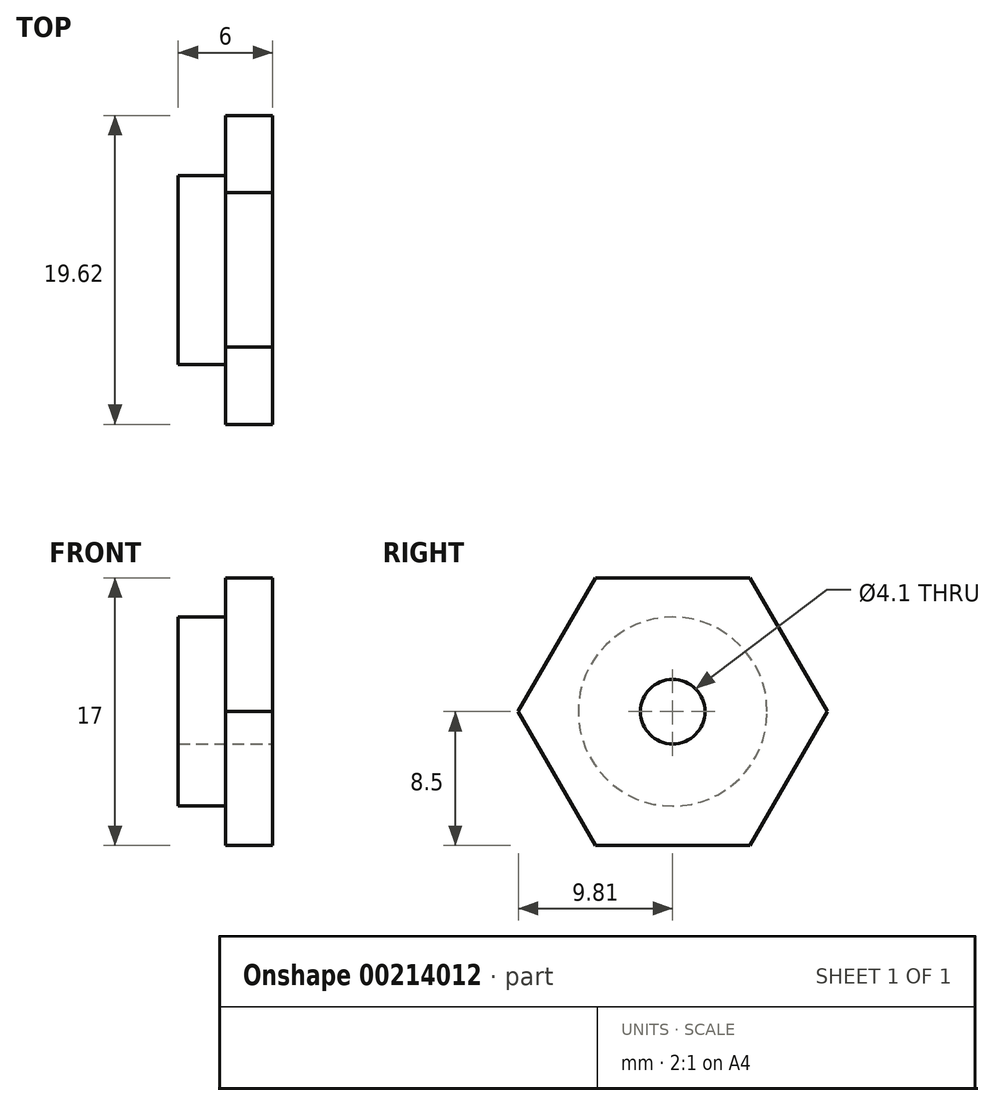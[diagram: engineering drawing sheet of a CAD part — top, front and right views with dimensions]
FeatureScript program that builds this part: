
annotation { "Feature Type Name" : "Feature", "Feature Type Description" : "" }
export const myFeature = defineFeature(function(context is Context, id is Id, definition is map)
    precondition{}
    {
        {
            var Q0;
            Q0=qCreatedBy(makeId("Right.planeOp"),FACE);
            var sketch = newSketch(context, id + "F0", { "sketchPlane" : qUnion([Q0])});
            skCircle(sketch, "E0", {"center": v(0, 0) * mm, "radius": 6 * mm});
            skSolve(sketch);
        }
        {
            var Q0;
            Q0 = qSketchRegion(id + "F0", true);
            extrude(context, id + "F1", {"entities" : qUnion([Q0]), "depth" : 3 * mm});
        }
        {
            var Q0;
            Q0=makeQuery(id+"F1.opExtrude","CAP_FACE",FACE,{"disambiguationData":[OSD([sQuery(id+"F0.wireOp",EDGE,"E0")])],"isStart":false});
            var sketch = newSketch(context, id + "F2", { "sketchPlane" : qUnion([Q0])});
            skCircle(sketch, "E1.cCircle", {"center": v(0, 0) * mm, "radius": 8.5 * mm, "construction": true});
            skLineSegment(sketch, "E1.0", {"start": v(-4.9, 8.5) * mm, "end": v(4.9, 8.5) * mm});
            skLineSegment(sketch, "E1.1", {"start": v(4.9, 8.5) * mm, "end": v(9.81, 0) * mm});
            skLineSegment(sketch, "E1.2", {"start": v(9.81, 0) * mm, "end": v(4.9, -8.5) * mm});
            skLineSegment(sketch, "E1.3", {"start": v(4.9, -8.5) * mm, "end": v(-4.9, -8.5) * mm});
            skLineSegment(sketch, "E1.4", {"start": v(-4.9, -8.5) * mm, "end": v(-9.81, 0) * mm});
            skLineSegment(sketch, "E1.5", {"start": v(-9.81, 0) * mm, "end": v(-4.9, 8.5) * mm});
            skPoint(sketch, "E1.0.midPoint", {"position": v(0, 8.5) * mm});
            skSolve(sketch);
        }
        {
            var Q0;
            Q0 = qSketchRegion(id + "F2", true);
            extrude(context, id + "F3", {"entities" : qUnion([Q0]), "operationType" : NewBodyOperationType.ADD, "depth" : 3 * mm});
        }
        {
            var Q0;
            Q0=makeQuery(id+"F3.opExtrude","CAP_FACE",FACE,{"disambiguationData":[OSD([sQuery(id+"F2.wireOp",EDGE,"E1.0"),sQuery(id+"F2.wireOp",EDGE,"E1.1"),sQuery(id+"F2.wireOp",EDGE,"E1.2"),sQuery(id+"F2.wireOp",EDGE,"E1.3"),sQuery(id+"F2.wireOp",EDGE,"E1.4"),sQuery(id+"F2.wireOp",EDGE,"E1.5")])],"isStart":false});
            var sketch = newSketch(context, id + "F4", { "sketchPlane" : qUnion([Q0])});
            skPoint(sketch, "E2", {"position": v(0, 0) * mm});
            skSolve(sketch);
        }
        {
            var Q0;
            Q0=sQuery(id+"F4.wireOp",VERTEX,"E2");
            var Q1;
            Q1=makeQuery(id+"F1.opExtrude","SWEPT_BODY",BODY,{"disambiguationData":[OSD([sQuery(id+"F0.wireOp",EDGE,"E0")])]});
            hole(context, id + "F5", {"style" : HoleStyle.SIMPLE, "endStyle" : HoleEndStyle.THROUGH, "standardTappedOrClearance" : lookupTablePath({ "standard" : "ISO", "engagement" : "75%", "pitch" : "0.9 mm", "size" : "M5", "type" : "Tapped" }), "standardBlindInLast" : lookupTablePath({ "standard" : "ISO", "engagement" : "75%", "pitch" : "0.9 mm", "size" : "M5", "type" : "Tapped" }), "holeDiameter" : 4.1 * mm, "locations" : qUnion([Q0]), "scope" : qUnion([Q1]), "isTappedThrough" : true, "showTappedDepth" : true});
        }
    });
